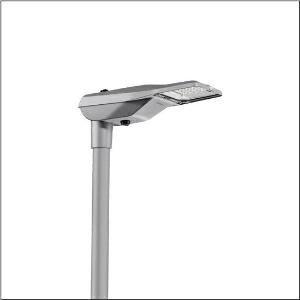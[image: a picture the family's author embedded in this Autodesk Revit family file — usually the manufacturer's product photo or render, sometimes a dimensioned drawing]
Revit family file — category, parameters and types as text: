
# Revit family: streetlight_sl_21_iq_micro___st1_5a_5xe1p31y08db_002f
name_source: partatom
category: Lighting Fixtures
units: mm (PartAtom-declared; Revit-internal decimal feet)

## family parameters
Cut with Voids When Loaded = No
Host = Face
Light Source = No
Part Type = Normal
Room Calculation Point = No
Round Connector Dimension = Use Diameter
Shared = No

## types (1)
- --- (1 x LED, 5030 lm, 39.1 W, 3000K)
    Apparent Load = 39 VA
    CIE Flux Codes = 22 53 95 100 100
    Color Rendering = 70
    Color Temperature = 3000K
    Default Elevation = 1800 mm
    Description = Streetlight SL 21 iQ micro, mast luminaire, primary light control with lens, of PMMA, primary optical cover: cover, of toughened safety glass, transparent, light distribution: ST1.5a, light emission: direct distribution, primary light characteristic: asymmetric, installation type: post-top, side-entry, LED, High Power LED, rated luminous flux: 5.030lm, luminous efficacy: 129lm/W, light colour: 730, colour temperature: 3000K, control: pre-setting: logarithmic dimming characteristic, Street-Remote, Auto-Match, Temp-Guard, Lumen-Switch, Night-Set, Smart-Wire, Light-Fading, Desk-Remote (wireless, voltage-free reading and setting of iQ features in the workshop via application-optimized NFC function/RFID function), optimised constant luminous flux control (CLO 2.0), mains connection: 220..240V, AC, 50/60Hz, start of lifetime: 39W, end of service life: 41W, reduction: 17W, luminaire housing, of diecast aluminium, powder-coated, Siteco® metallic grey (DB 702S), corrosivity category C5 mid according to DIN EN ISO 12944, please order mast flange separately, inclination adjustable: 0°, 5°, 10°, 15°, sealing non-destructively replaceable, multi-level sealing system, length: 528mm, width: 235mm, height: 110mm, mast flange for spigot size: 42mm (side-entry): 5XC10008XM4, 60/48mm (side-entry/post-top): 5XC10108XM2, 76/60mm (side-entry/post-top): 5XC10108XM1, Smart Interface below and above, protection rating (complete): IP66, insulation class (complete): insulation class II (safety insulation), certification: CE, ENEC, ENEC+, VDE, impact resistance: IK09, permissible operating ambient temperature for outdoor applications: -40..+50°C, standard-compliant lighting for roads and squares, packaging unit: 1 piece

Light Distribution: ST1.5a
    Height = 110 mm
    Lamp = 1 x LED
    Lamp Light Flux = 5030 lm
    Lamp Power = 39.1 W
    Lamp count = 1
    Length = 528 mm
    Luminous efficacy = 129 lm/W
    Manufacturer = Siteco
    ModVariant = No
    Model = 5XE1P31Y08DB
    Number of Poles = 1
    OnlyDefault = Yes
    Power Factor = 1
    Product Name = Streetlight SL 21 iQ micro | ST1.5a
    Product group = mast luminaire | pylon top
    ProductGroupID = 6100
    Protection Class = Protection class II
    Protection Degree = IP 66
    RLX_Detail_Level = 1
    RLX_Emergency_Light_Flux = 0 lm
    RLX_Emergency_Type = 0
    RLX_Emergency_Type_DB = No
    RlxData = <blob elided: 102749 chars, md5=ea2b1418>
    Socket = socket
    Standby Power = 0 W
    System Light Flux = 5030 lm
    System Power = 39 W
    Type Comments = factory setting: luminous flux: 100 % | dim-lin: 254 | 765 mA
    Type Image = l_1007239.jpg
    URL = http://relux.com
    VarID = @adj_080829
    Voltage = 0 V
    Weight = 0.00 kg
    Width = 235 mm

## geometry (parser evidence)
native form markers: Blend x4, Sweep x11
no freeform markers — native parametric forms only
